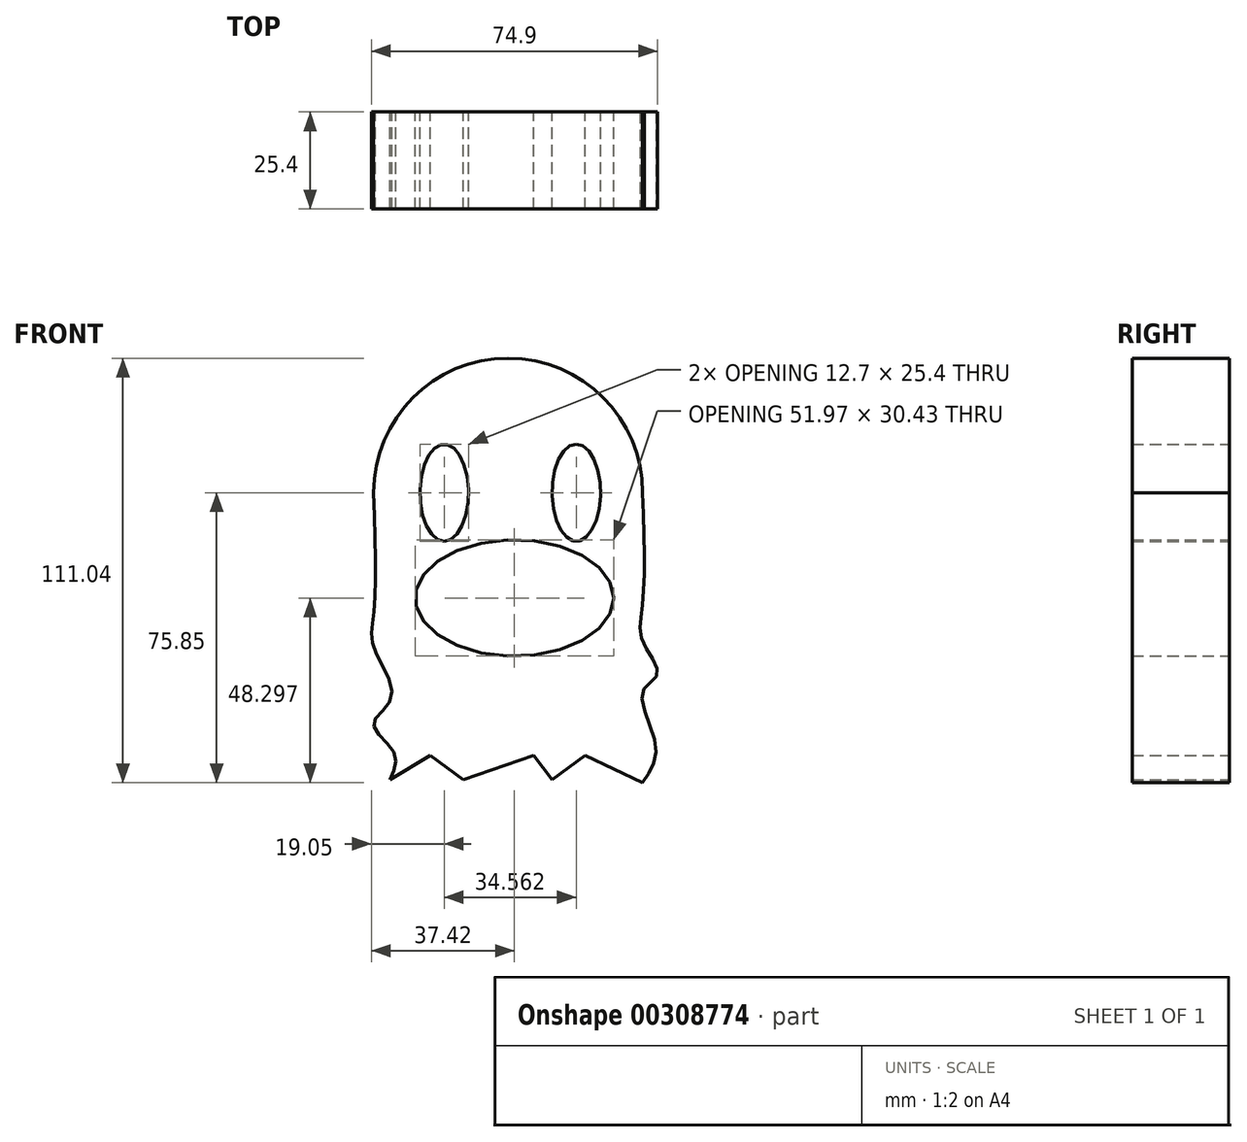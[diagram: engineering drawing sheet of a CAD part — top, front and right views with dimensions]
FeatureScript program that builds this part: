
annotation { "Feature Type Name" : "Feature", "Feature Type Description" : "" }
export const myFeature = defineFeature(function(context is Context, id is Id, definition is map)
    precondition{}
    {
        {
            var Q0;
            Q0=qCreatedBy(makeId("Front.planeOp"),FACE);
            var sketch = newSketch(context, id + "F0", { "sketchPlane" : qUnion([Q0])});
            skArc(sketch, "E0", {"start": v(33.54, 0) * mm, "mid": v(-1.65, 35.19) * mm, "end": v(-36.84, 0) * mm});
            skFitSpline(sketch, "E1", {"points": [v(-36.84, 0) * mm, v(-36.84, -31.76) * mm, v(-36.84, -40.48) * mm, v(-32.15, -53.57) * mm, v(-36.84, -60.46) * mm, v(-31.46, -68.04) * mm, v(-32.6, -75.16) * mm], "startDerivative": vector(4.2, -138.76) * mm, "endDerivative": vector(-26.53, -55.75) * mm});
            skFitSpline(sketch, "E2", {"points": [v(33.54, 0) * mm, v(33.54, -29) * mm, v(33.54, -38.88) * mm, v(37.43, -47.37) * mm, v(33.54, -52.2) * mm, v(36.97, -66.43) * mm, v(33.54, -75.85) * mm], "startDerivative": vector(4.36, -129.17) * mm, "endDerivative": vector(-38.56, -55.45) * mm});
            skLineSegment(sketch, "E3", {"start": v(-32.6, -75.16) * mm, "end": v(-22.04, -68.73) * mm});
            skLineSegment(sketch, "E4", {"start": v(-22.04, -68.73) * mm, "end": v(-13.32, -75.16) * mm});
            skLineSegment(sketch, "E5", {"start": v(-13.32, -75.16) * mm, "end": v(5.05, -68.73) * mm});
            skLineSegment(sketch, "E6", {"start": v(5.05, -68.73) * mm, "end": v(9.87, -75.16) * mm});
            skLineSegment(sketch, "E7", {"start": v(9.87, -75.16) * mm, "end": v(18.45, -68.73) * mm});
            skLineSegment(sketch, "E8", {"start": v(18.45, -68.73) * mm, "end": v(33.54, -75.85) * mm});
            skEllipse(sketch, "E9", {"center": v(-18.37, 0) * mm, "majorRadius": 12.7 * mm, "minorRadius": 6.35 * mm, "majorAxis": v(0, -1)});
            skEllipse(sketch, "E10", {"center": v(16.2, 0) * mm, "majorRadius": 12.7 * mm, "minorRadius": 6.35 * mm, "majorAxis": v(0, 1)});
            skEllipse(sketch, "E11", {"center": v(0, -27.55) * mm, "majorRadius": 15.21 * mm, "minorRadius": 25.98 * mm, "majorAxis": v(0, -1)});
            skSolve(sketch);
        }
        {
            var Q0;
            Q0=makeQuery(id+"F0.imprint","IMPRINT",FACE,{"disambiguationData":[TD([[makeQuery(id+"F0.imprint","IMPRINT",EDGE,{"derivedFrom":sQuery(id+"F0.wireOp",EDGE,"E0")}),1.0]])]});
            extrude(context, id + "F1", {"entities" : qUnion([Q0]), "depth" : 25.4 * mm});
        }
    });
